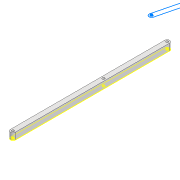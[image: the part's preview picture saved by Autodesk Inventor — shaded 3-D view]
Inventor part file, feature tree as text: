
AUTODESK INVENTOR PART (.ipt)
format: ipt  version: 2022 (Build 260153000, 153)  size: 96,256 bytes
history: native  units: mm
features: sketch x2, extrude x1, projected_geometry x1
ambient origin geometry x8: Origin, YZ Plane, XZ Plane, XY Plane, X Axis, Y Axis, Z Axis, Center Point
bodies: Solid1 (feature_tree)
feature tree (4):
  extrude  "Extrusion1"  Depth=6.0mm
  sketch  "Sketch2"  dims[d2=3.0mm d3=3.0mm d4=8.0mm d5=0.0mm d6=3.0mm d7=111.208mm]
  sketch  "Sketch1"  dims[d0=189.323mm d1=6.0mm]
  projected_geometry  "Projected Loop1"
